# Revit family: Thermoscreens_MechanicalEquipment_AirCurtains_JetOverdoorHeaterx
name_source: partatom
category: Mechanical Equipment
units: mm (PartAtom-declared; Revit-internal decimal feet)

## family parameters
Classification = None
Cut with Voids When Loaded = Yes
Host = Face
Part Type = Normal
Room Calculation Point = No
Round Connector Dimension = Use Diameter
Shared = No

## types (1)
- Jet 3
    A = 602 mm  [stored 1.97507 ft]
    Assembly Code = D3090400
    AssetType = Fixed
    B = 428 mm  [stored 1.4042 ft]
    BIMObjectName = Thermoscreens_MechanicalEquipment_OverdoorHeater_JetOverdoorHeater_Jet3
    ClassificationName = Uniclass2015
    ClassificationValue = Pr_70_60_36_02
    Color = RAL 9016
    Default Elevation = 0 mm  [stored 0 ft]
    Depth = 120 mm  [stored 0.393701 ft]
    Description = Lot 20 compliant, intelligent and energy saving the Jet overdoor heater provides warmth and comfort to the surrounding area. This makes it an ideal solution for doorways that are not used regularly and are normally kept shut.
    DocumentationCertificates = https://www.bimstore.co
    DocumentationInstallationGuide = https://www.bimstore.co
    DocumentationLiterature = https://www.bimstore.co
    DocumentationMaintenance = https://www.bimstore.co
    DocumentationTechnical = https://www.bimstore.co
    DurationUnit = Year
    ElectricalInput = 3030 W
    ExpectedLife = 0
    Features = - Lot 20 compliant
- Seven-day timer
- Electric heating
- Remote controlled
- 1 year warranty
- 600mm wide
- Up to 2.3m mounting height
- Standard RAL 9016 (white)
- Two heat settings
- IP20 rated
- ‘Fan only’ option to recirculate air in Summer
    HeatOutput = 1.5 / 3.0 kW
    Height = 201 mm  [stored 0.659449 ft]
    IfcExportAs = IfcUnitaryEquipmentType
    IfcExportType = AIRCONDITIONINGUNIT
    Keynote = U
    Length = 602 mm  [stored 1.97507 ft]
    Manufacturer = Thermoscreens
    ManufacturerName = Thermoscreens
    MaximumAirVolume = 200 m3/h
    MaximumVelocity = 6.0 m/s
    Model = Jet 3
    ModelNumber = Jet 3
    ModelReference = Thermoscreens Jet Series Intelligent Overdoor Heater
    NBSDescription = Overdoor Heater
    NBSObjectName = Thermoscreens - Overdoor Heater
    NBSReference = 90-40-35/310
    NoiseOutput = 46.5 dB(A) @3m
    NominalDepth = 120 mm  [stored 0.393701 ft]
    NominalHeight = 201 mm  [stored 0.659449 ft]
    NominalLength = 602 mm  [stored 1.97507 ft]
    ProductionYear = 2022
    Size = 600 x 120 x 201mm
    Supply = 230V~1P&N
    Type Comments = Thermoscreens Jet Series Intelligent Overdoor Heater
    TypeName = Thermoscreens Jet Series Intelligent Overdoor Heater
    TypeOfHeating = Electric
    URL = https://thermoscreens.com
    WarrantyDurationLabor = 0
    WarrantyDurationParts = 0
    WarrantyDurationUnit = Year
    Weight = 4.50 kg
    _BSBibleVersion = 16
    _BimSpecGuid = 0
    _CurrentRevision = 1
    _DistributedBy = www.bimstore.co
    _ObjectUserGuide = https://www.bimstore.co

note: [stored X ft] marks values corroborated as IEEE doubles in the binary element streams (Revit-internal decimal feet)

## geometry (parser evidence)
native form markers: Sweep x3
no freeform markers — native parametric forms only
